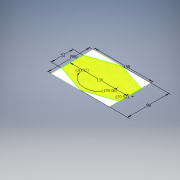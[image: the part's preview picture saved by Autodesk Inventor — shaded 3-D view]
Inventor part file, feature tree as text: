
AUTODESK INVENTOR PART (.ipt)
format: ipt  version: 2016 (Build 200138000, 138)  size: 109,056 bytes
history: native  units: mm
features: sketch x1, other x1
ambient origin geometry x8: Origin, YZ Plane, XZ Plane, XY Plane, X Axis, Y Axis, Z Axis, Center Point
feature tree (2):
  sketch  "Sketch1"  dims[d1=136.0mm d2=98.0mm d6=136.0mm d7=98.000008mm d18=52.0mm d28=3.652014mm d29=3.652014mm d30=27.763911mm]
  other  "Image1"
